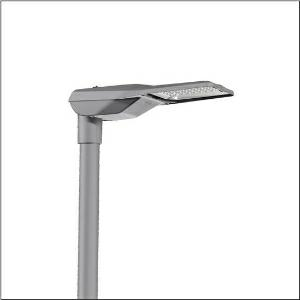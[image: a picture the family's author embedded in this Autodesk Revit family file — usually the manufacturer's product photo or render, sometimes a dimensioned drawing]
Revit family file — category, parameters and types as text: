
# Revit family: streetlight_sl_21_mini___st1_0a_5xe2d43s08jb_d214
name_source: partatom
category: Lighting Fixtures
units: mm (PartAtom-declared; Revit-internal decimal feet)

## family parameters
Cut with Voids When Loaded = No
Host = Face
Light Source = No
Part Type = Normal
Room Calculation Point = No
Round Connector Dimension = Use Diameter
Shared = No

## types (1)
- --- (1 x LED, 13500 lm, 88.6 W, 4000K)
    Apparent Load = 89 VA
    CIE Flux Codes = 40 73 97 100 100
    Color Rendering = 70
    Color Temperature = 4000K
    Default Elevation = 1800 mm
    Description = Streetlight SL 21 mini, mast luminaire, primary light control with lens, of PMMA, primary optical cover: cover, of toughened safety glass, transparent, light distribution: ST1.0a, light emission: direct distribution, primary light characteristic: asymmetric, installation type: side-entry, post-top, LED, High Power LED, rated luminous flux: 13.500lm, luminous efficacy: 152lm/W, light colour: 740, colour temperature: 4000K, control gear: D4i, control: overheat protection, constant luminous flux control, time-dependent luminous flux control, flexible luminous flux parameterisation, pre-setting: logarithmic dimming characteristic, mains connection: 220..240V, AC, 50/60Hz, start of lifetime: 89W, end of service life: 92W, reduction: 41W, luminaire housing, of diecast aluminium, powder-coated, SITECO metallic grey (DB 702S), corrosivity category C5 high according to DIN EN ISO 12944, please order mast flange separately, inclination adjustable: 0°, 5°, 10°, 15°, sealing non-destructively replaceable, multi-level sealing system, length: 628mm, width: 235mm, height: 110mm, mast flange for spigot size: 42mm (side-entry): 5XC10008XM4, 60/48mm (side-entry/post-top): 5XC10108XM2, 76/60mm (side-entry/post-top): 5XC10108XM1, mounting height: 4..8m, Smart Interface above, protection rating (complete): IP66, insulation class (complete): insulation class II (safety insulation), certification: CE, ENEC, ENEC+, VDE, impact resistance: IK10, permissible operating ambient temperature for outdoor applications: -40..+50°C, standard-compliant lighting for roads and squares, packaging unit: 1 piece

Light Distribution: ST1.0a
    Height = 110 mm
    Lamp = 1 x LED
    Lamp Light Flux = 13500 lm
    Lamp Power = 88.6 W
    Lamp count = 1
    Length = 625 mm
    Luminous efficacy = 152 lm/W
    Manufacturer = Siteco
    ModVariant = No
    Model = 5XE2D43S08JB
    Number of Poles = 1
    OnlyDefault = Yes
    Power Factor = 1
    Product Name = Streetlight SL 21 mini | ST1.0a
    Product group = mast luminaire | pylon top
    ProductGroupID = 6100
    Protection Class = Protection class II
    Protection Degree = IP 66
    RLX_Detail_Level = 1
    RLX_Emergency_Light_Flux = 0 lm
    RLX_Emergency_Type = 0
    RLX_Emergency_Type_DB = No
    RlxData = <blob elided: 26281 chars, md5=fbebc262>
    Socket = socket
    Standby Power = 0 W
    System Light Flux = 13500 lm
    System Power = 89 W
    Type Comments = factory setting: luminous flux: 100 % | dim-lin: 254 | 915 mA
    Type Image = l_1003515.jpg
    URL = http://relux.com
    VarID = @adj_031387
    Voltage = 0 V
    Weight = 0.00 kg
    Width = 234 mm

## geometry (parser evidence)
native form markers: Blend x4, Sweep x11
no freeform markers — native parametric forms only
